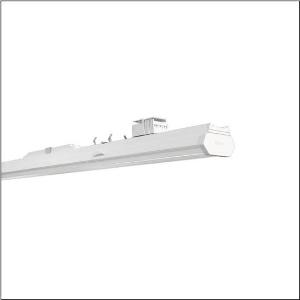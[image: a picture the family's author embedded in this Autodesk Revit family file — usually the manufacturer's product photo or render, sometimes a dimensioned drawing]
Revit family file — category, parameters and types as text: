
# Revit family: licross_r__11_protected_ho_51td12dn4fxm3s4_da94
name_source: partatom
category: Lighting Fixtures
units: mm (PartAtom-declared; Revit-internal decimal feet)

## family parameters
Cut with Voids When Loaded = No
Host = Face
Light Source = No
Part Type = Normal
Room Calculation Point = No
Round Connector Dimension = Use Diameter
Shared = No

## types (1)
- --- (1 x LED, 970 lm, 7.4 W, 4000K)
    Apparent Load = 7 VA
    CIE Flux Codes = 70 91 97 98 100
    Color Rendering = 80
    Color Temperature = 4000K
    Default Elevation = 1800 mm
    Description = Licross® 11 Protected HO, luminaire insert, of sheet steel, galvanised, coil coated, white, length: 1.500mm, width: 90mm, height: 101mm, LED rated luminous flux: 15.270lm, light colour: 840, control gear: DALI 2, with plug, 6-pole, with phase selection, for trunking rail, 9 or 11-core, mains connection: 220..240V, AC, 50/60Hz, rated input power: 91W, for trunking rail, 9-/11-core, halogen-free wiring, for emergency light function, converter,control gear: single battery element, battery: LiFePO4, 9Ah, primary light control with lens, of plastic, primary optical cover: cover, of PMMA, light emission: direct distribution, primary light characteristic: symmetric, protection rating (complete): IP54, insulation class (complete): insulation class I (protective earthing), certification: CE, UKCA, protection symbol: D if used in an environment with non-conductive dust loads with corresponding accessories, impact resistance: IK06, permissible ambient temperature for indoor applications: +5..+30°C, standard: EN 60598-2-22, LABS conformity tested according to VDMA 24364:2018-05, reducing of maximum allowable ambient temperature of 5°C with ceiling mounting, corresponds to IFS (International Featured Standards) requirements for safety and quality in the food industry, packaging unit: 1 piece
    Height = 92 mm
    Lamp = 1 x LED
    Lamp Light Flux = 970 lm
    Lamp Power = 7.4 W
    Lamp count = 1
    Length = 1500 mm
    Luminous efficacy = 131 lm/W
    Manufacturer = Siteco
    ModVariant = No
    Model = 51TD12DN4FXM3S4
    Mounting Place = Ceiling
    Mounting Type = Pendant
    Number of Poles = 1
    OnlyDefault = Yes
    Power Factor = 1
    Product Name = Licross® 11 Protected HO
    Product group = luminaire insert
    ProductGroupID = 901
    Protection Class = Protection class I
    Protection Degree = IP 54
    RLX_Detail_Level = 1
    RLX_Emergency_Light_Flux = 0 lm
    RLX_Emergency_Type = 0
    RLX_Emergency_Type_DB = No
    RlxData = <blob elided: 24941 chars, md5=7590e954>
    Socket = socket
    Standby Power = 0 W
    System Light Flux = 970 lm
    System Power = 7 W
    Type Comments = : emergency light operation: 3 h
    Type Image = l_1256145.jpg
    URL = http://relux.com
    VarID = @adj_059621
    Voltage = 0 V
    Weight = 0.00 kg
    Width = 88 mm

## geometry (parser evidence)
native form markers: Blend x4, Sweep x13
no freeform markers — native parametric forms only
